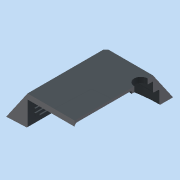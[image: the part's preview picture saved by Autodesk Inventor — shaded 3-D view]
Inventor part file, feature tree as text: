
AUTODESK INVENTOR PART (.ipt)
format: ipt  version: 2015 (Build 190159000, 159)  size: 671,232 bytes
history: native  units: in
note: dims shown in document units (in); Inventor stores cm internally (conversion verified against a paired STEP export)
features: split x5, other x3, plane x3
ambient origin geometry x8: Origin, YZ Plane, XZ Plane, XY Plane, X Axis, Y Axis, Z Axis, Center Point
bodies: Solid1 (feature_tree), Solid2 (feature_tree), Solid3 (feature_tree), Solid12 (feature_tree), Solid13 (feature_tree), Solid14 (feature_tree), Solid15 (feature_tree), Solid16 (feature_tree), Solid17 (feature_tree), Solid18 (feature_tree), Solid19 (feature_tree)
feature tree (11):
  other  "BatteryEnclosure.ipt"
  plane  "Work Plane1"
  plane  "Work Plane3"
  split  "Split1"
  split  "Split2"
  split  "Split3"
  split  "Split4"
  split  "Split5"
  other  "Solid2::BatteryEnclosure.ipt"
  other  "TaggingFeature1"
  plane  "Work Plane2"
